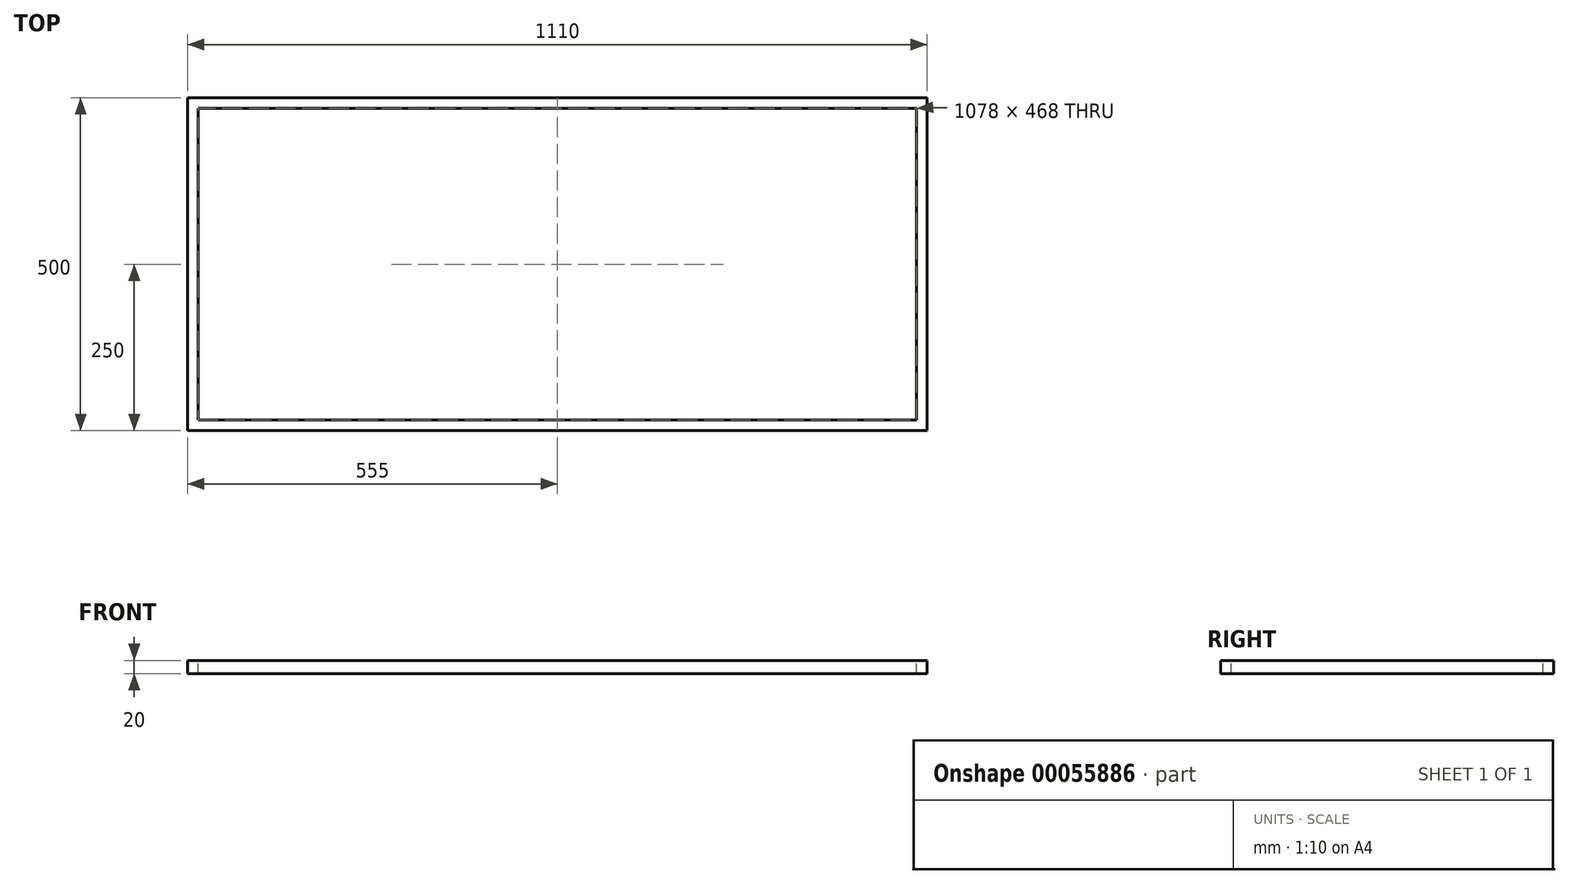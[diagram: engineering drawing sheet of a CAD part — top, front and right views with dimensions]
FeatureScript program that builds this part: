
annotation { "Feature Type Name" : "Feature", "Feature Type Description" : "" }
export const myFeature = defineFeature(function(context is Context, id is Id, definition is map)
    precondition{}
    {
        {
            var Q0;
            Q0=qCreatedBy(makeId("Top.planeOp"),FACE);
            var sketch = newSketch(context, id + "F0", { "sketchPlane" : qUnion([Q0])});
            skLineSegment(sketch, "E0.rect.bottom", {"start": v(-555, 250) * mm, "end": v(555, 250) * mm});
            skLineSegment(sketch, "E0.rect.top", {"start": v(-555, -250) * mm, "end": v(555, -250) * mm});
            skLineSegment(sketch, "E0.rect.left", {"start": v(-555, 250) * mm, "end": v(-555, -250) * mm});
            skLineSegment(sketch, "E0.rect.right", {"start": v(555, 250) * mm, "end": v(555, -250) * mm});
            skPoint(sketch, "E0.rect.middle", {"position": v(0, 0) * mm});
            skLineSegment(sketch, "E1.0", {"start": v(-539, 234) * mm, "end": v(539, 234) * mm});
            skLineSegment(sketch, "E1.1", {"start": v(-539, 234) * mm, "end": v(-539, -234) * mm});
            skLineSegment(sketch, "E1.2", {"start": v(-539, -234) * mm, "end": v(539, -234) * mm});
            skLineSegment(sketch, "E1.3", {"start": v(539, 234) * mm, "end": v(539, -234) * mm});
            skSolve(sketch);
        }
        {
            var Q0;
            Q0=makeQuery(id+"F0.imprint","IMPRINT",FACE,{"disambiguationData":[TD([[makeQuery(id+"F0.imprint","IMPRINT",EDGE,{"derivedFrom":sQuery(id+"F0.wireOp",EDGE,"E0.rect.bottom")}),-1.0]])]});
            extrude(context, id + "F1", {"entities" : qUnion([Q0]), "oppositeDirection" : true, "depth" : 20 * mm});
        }
    });
